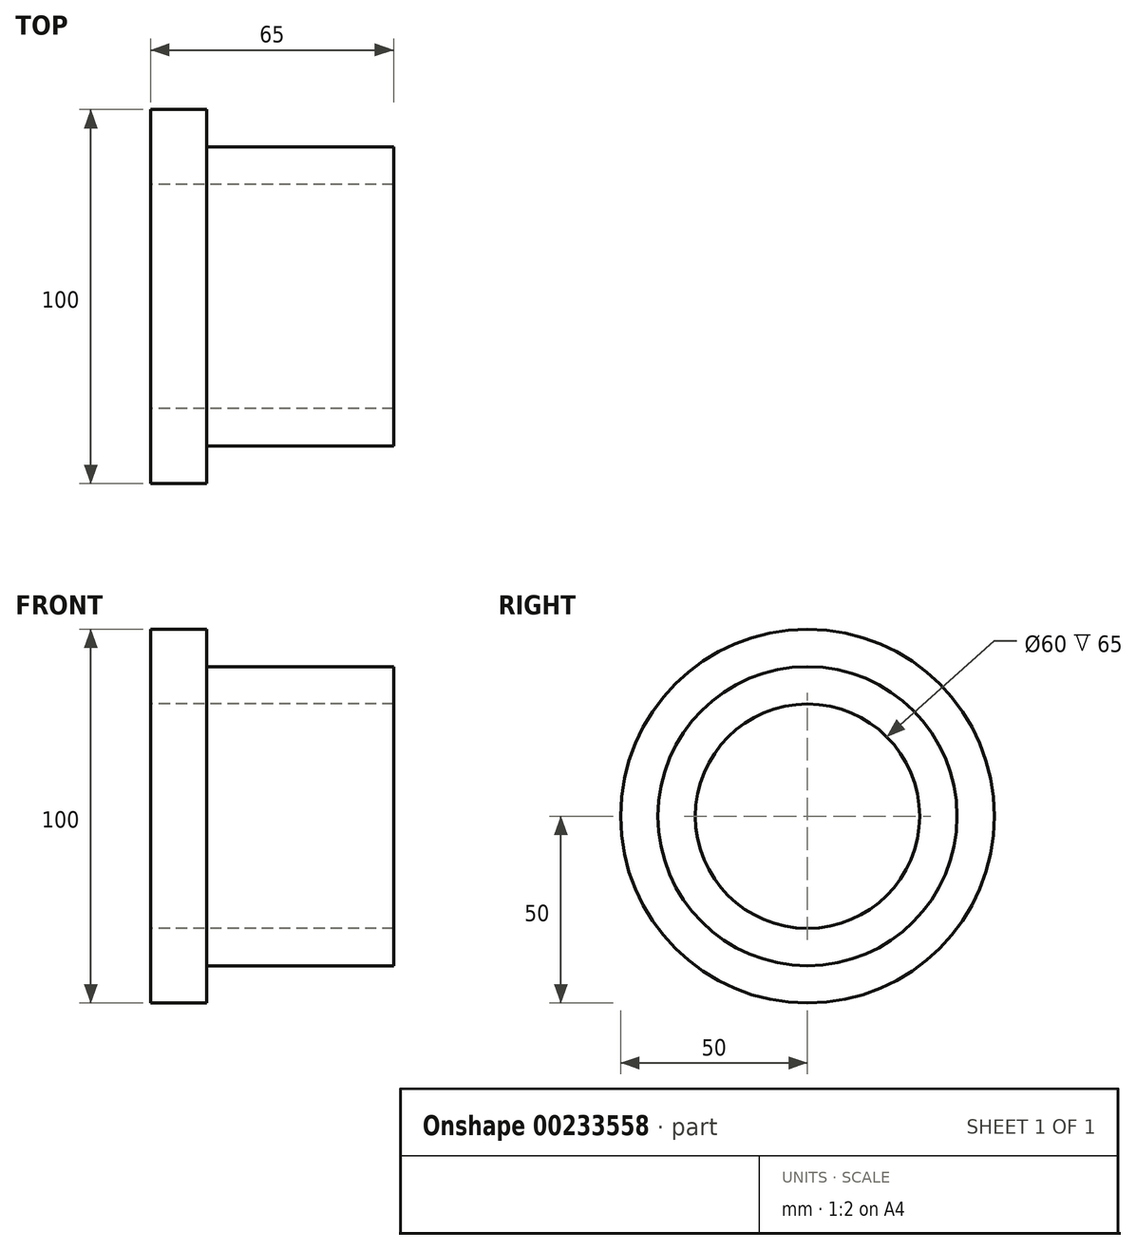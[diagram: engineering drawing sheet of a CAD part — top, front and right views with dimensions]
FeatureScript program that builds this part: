
annotation { "Feature Type Name" : "Feature", "Feature Type Description" : "" }
export const myFeature = defineFeature(function(context is Context, id is Id, definition is map)
    precondition{}
    {
        {
            var Q0;
            Q0=qCreatedBy(makeId("Right.planeOp"),FACE);
            var sketch = newSketch(context, id + "F0", { "sketchPlane" : qUnion([Q0])});
            skCircle(sketch, "E0", {"center": v(0, 0) * mm, "radius": 40 * mm});
            skCircle(sketch, "E1", {"center": v(0, 0) * mm, "radius": 30 * mm});
            skCircle(sketch, "E2", {"center": v(0, 0) * mm, "radius": 50 * mm});
            skSolve(sketch);
        }
        {
            var Q0;
            Q0=makeQuery(id+"F0.imprint","IMPRINT",FACE,{"disambiguationData":[TD([[makeQuery(id+"F0.imprint","IMPRINT",EDGE,{"derivedFrom":sQuery(id+"F0.wireOp",EDGE,"E0")}),-1.0]])]});
            var Q1;
            Q1=makeQuery(id+"F0.imprint","IMPRINT",FACE,{"disambiguationData":[TD([[makeQuery(id+"F0.imprint","IMPRINT",EDGE,{"derivedFrom":sQuery(id+"F0.wireOp",EDGE,"E0")}),1.0]])]});
            extrude(context, id + "F1", {"entities" : qUnion([Q0, Q1]), "depth" : 15 * mm});
        }
        {
            var Q0;
            Q0=makeQuery(id+"F0.imprint","IMPRINT",FACE,{"disambiguationData":[TD([[makeQuery(id+"F0.imprint","IMPRINT",EDGE,{"derivedFrom":sQuery(id+"F0.wireOp",EDGE,"E0")}),1.0]])]});
            extrude(context, id + "F2", {"entities" : qUnion([Q0]), "operationType" : NewBodyOperationType.ADD, "depth" : 65 * mm});
        }
    });
